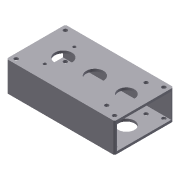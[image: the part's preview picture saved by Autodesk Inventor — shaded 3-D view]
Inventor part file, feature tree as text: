
AUTODESK INVENTOR PART (.ipt)
format: ipt  version: 2015 (Build 190159000, 159)  size: 173,056 bytes
history: native  units: in
note: dims shown in document units (in); Inventor stores cm internally (conversion verified against a paired STEP export)
features: other x1, imported_body x1, sketch x1
ambient origin geometry x8: Origin, YZ Plane, XZ Plane, XY Plane, X Axis, Y Axis, Z Axis, Center Point
bodies: Body1 (feature_tree)
feature tree (3):
  other  "Toughbox-nano-d01"
  imported_body  "Base1"
  sketch  "Sketch1"
